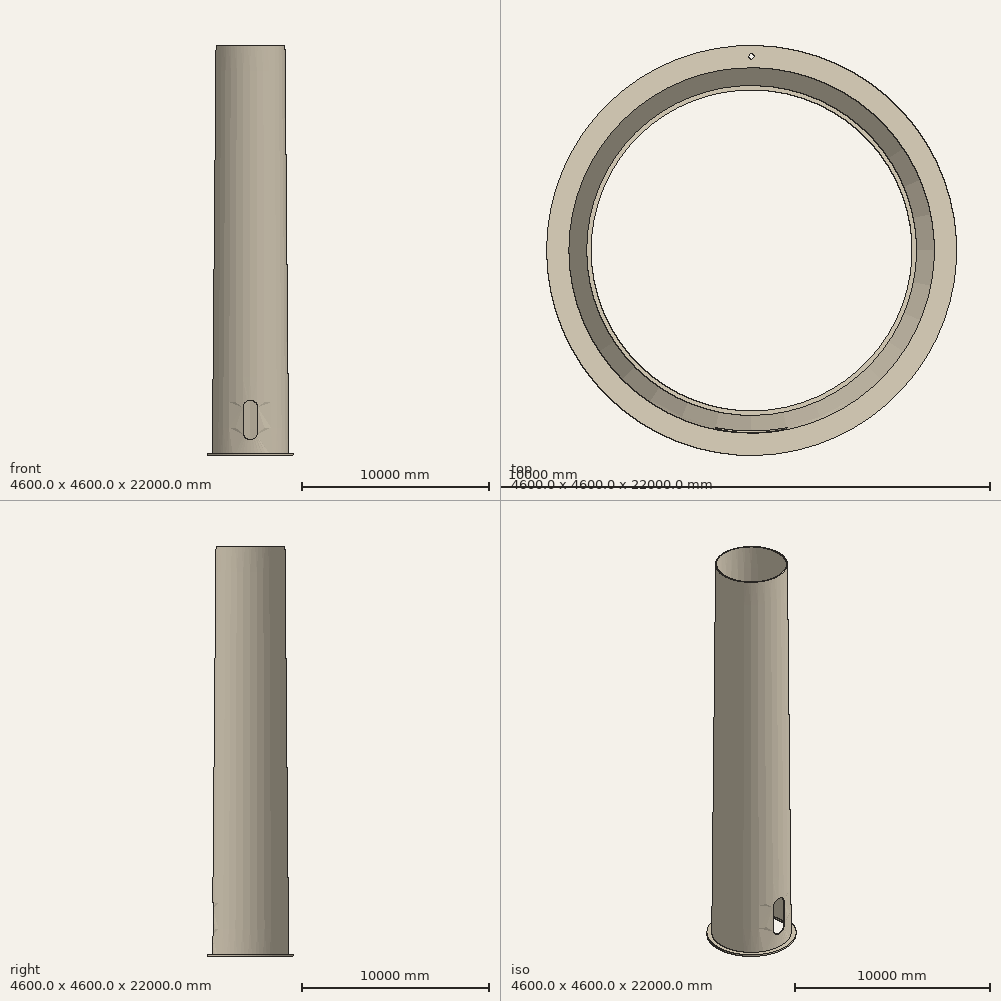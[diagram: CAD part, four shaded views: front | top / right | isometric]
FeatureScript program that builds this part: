
annotation { "Feature Type Name" : "Feature", "Feature Type Description" : "" }
export const myFeature = defineFeature(function(context is Context, id is Id, definition is map)
    precondition{}
    {
        {
            var Q0;
            Q0=qCreatedBy(makeId("Front.planeOp"),FACE);
            var sketch = newSketch(context, id + "F0", { "sketchPlane" : qUnion([Q0])});
            skLineSegment(sketch, "E0", {"start": v(0, 0) * mm, "end": v(0, 22000) * mm, "construction": true});
            skLineSegment(sketch, "E1.bottom", {"start": v(2000, 0) * mm, "end": v(2300, 0) * mm});
            skLineSegment(sketch, "E1.top", {"start": v(2050, 100) * mm, "end": v(2300, 100) * mm});
            skLineSegment(sketch, "E1.left", {"start": v(2000, 0) * mm, "end": v(2000, 100) * mm});
            skLineSegment(sketch, "E1.right", {"start": v(2300, 0) * mm, "end": v(2300, 100) * mm});
            skLineSegment(sketch, "E2.bottom", {"start": v(1800, 22000) * mm, "end": v(1850, 22000) * mm});
            skLineSegment(sketch, "E3", {"start": v(1800, 22000) * mm, "end": v(2000, 100) * mm});
            skLineSegment(sketch, "E4.0", {"start": v(1850, 22000) * mm, "end": v(2050, 100) * mm});
            skSolve(sketch);
        }
        {
            var Q0;
            Q0 = qSketchRegion(id + "F0", true);
            var Q1;
            Q1=sQuery(id+"F0.wireOp",EDGE,"E0");
            revolve(context, id + "F1", {"entities" : qUnion([Q0]), "axis" : qUnion([Q1]), "revolveType" : RevolveType.FULL});
        }
        {
            var Q0;
            Q0=makeQuery(id+"F1.opRevolve","SWEPT_FACE",FACE,{"disambiguationData":[OSD([sQuery(id+"F0.wireOp",EDGE,"E1.bottom")])]});
            var sketch = newSketch(context, id + "F2", { "sketchPlane" : qUnion([Q0])});
            skCircle(sketch, "E5", {"center": v(0, -2175) * mm, "radius": 30 * mm});
            skSolve(sketch);
        }
        {
            var Q0;
            Q0 = qSketchRegion(id + "F2", true);
            extrude(context, id + "F3", {"entities" : qUnion([Q0]), "operationType" : NewBodyOperationType.REMOVE, "endBound" : BoundingType.UP_TO_NEXT, "oppositeDirection" : true, "depth" : 25 * mm});
        }
        {
            var Q0;
            Q0=qCreatedBy(makeId("Front.planeOp"),FACE);
            var sketch = newSketch(context, id + "F4", { "sketchPlane" : qUnion([Q0])});
            skLineSegment(sketch, "E6.bottom", {"start": v(400, 1250) * mm, "end": v(-400, 1250) * mm, "construction": true});
            skLineSegment(sketch, "E6.top", {"start": v(400, 2550) * mm, "end": v(-400, 2550) * mm, "construction": true});
            skLineSegment(sketch, "E6.left", {"start": v(400, 1250) * mm, "end": v(400, 2550) * mm});
            skLineSegment(sketch, "E6.right", {"start": v(-400, 1250) * mm, "end": v(-400, 2550) * mm});
            skPoint(sketch, "E6.middle", {"position": v(0, 1900) * mm});
            skArc(sketch, "E7", {"start": v(400, 2550) * mm, "mid": v(0, 2950) * mm, "end": v(-400, 2550) * mm});
            skArc(sketch, "E8", {"start": v(-400, 1250) * mm, "mid": v(0, 850) * mm, "end": v(400, 1250) * mm});
            skSolve(sketch);
        }
        {
            var Q0;
            Q0=makeQuery(id+"F4.imprint","IMPRINT",FACE,{"disambiguationData":[TD([[makeQuery(id+"F4.imprint","IMPRINT",EDGE,{"derivedFrom":sQuery(id+"F4.wireOp",EDGE,"E6.left")}),1.0]])]});
            extrude(context, id + "F5", {"entities" : qUnion([Q0]), "operationType" : NewBodyOperationType.REMOVE, "depth" : 2500 * mm});
        }
    });
